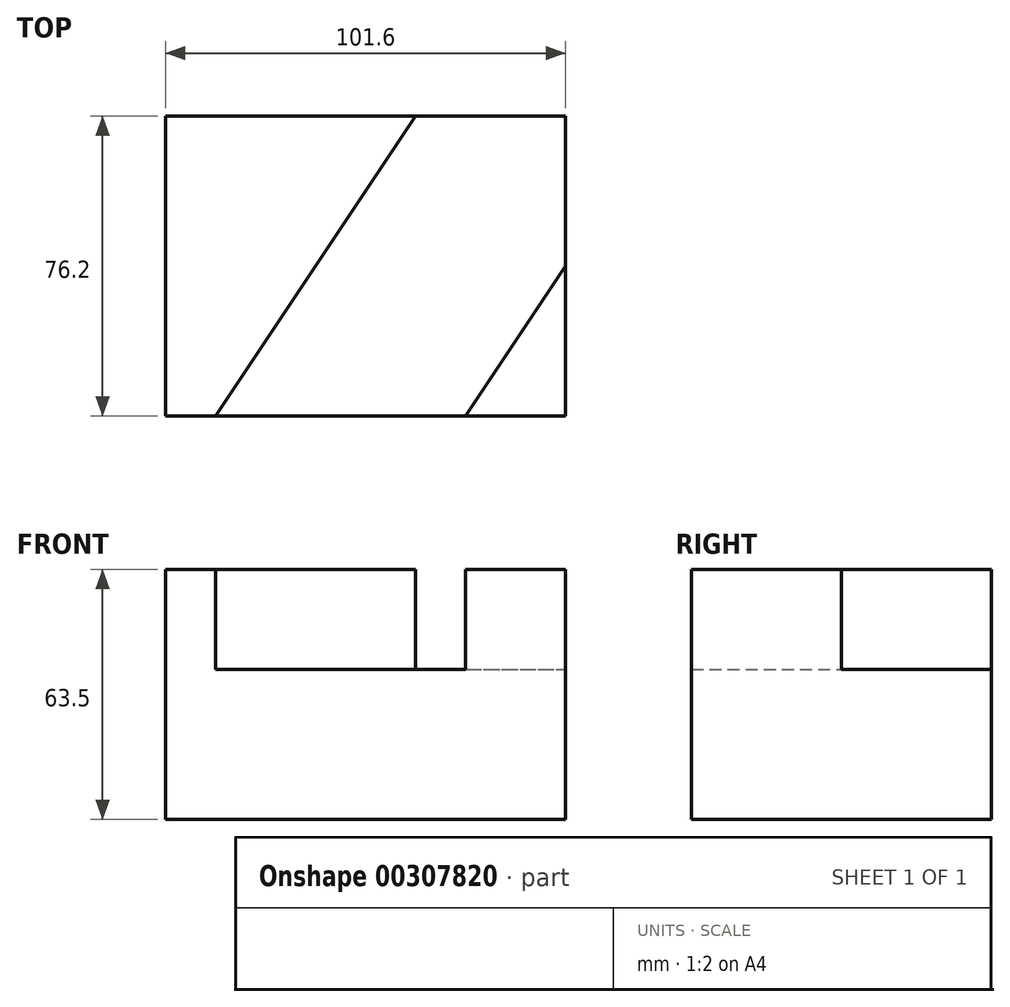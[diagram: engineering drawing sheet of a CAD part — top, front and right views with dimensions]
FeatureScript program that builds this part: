
annotation { "Feature Type Name" : "Feature", "Feature Type Description" : "" }
export const myFeature = defineFeature(function(context is Context, id is Id, definition is map)
    precondition{}
    {
        {
            var Q0;
            Q0=qCreatedBy(makeId("Top.planeOp"),FACE);
            var sketch = newSketch(context, id + "F0", { "sketchPlane" : qUnion([Q0])});
            skLineSegment(sketch, "E0.bottom", {"start": v(-43.22, 25.25) * mm, "end": v(58.38, 25.25) * mm});
            skLineSegment(sketch, "E0.top", {"start": v(-43.22, -50.95) * mm, "end": v(58.38, -50.95) * mm});
            skLineSegment(sketch, "E0.left", {"start": v(-43.22, 25.25) * mm, "end": v(-43.22, -50.95) * mm});
            skLineSegment(sketch, "E0.right", {"start": v(58.38, 25.25) * mm, "end": v(58.38, -50.95) * mm});
            skSolve(sketch);
        }
        {
            var Q0;
            Q0=makeQuery(id+"F0.imprint","IMPRINT",FACE,{"disambiguationData":[TD([[makeQuery(id+"F0.imprint","IMPRINT",EDGE,{"derivedFrom":sQuery(id+"F0.wireOp",EDGE,"E0.bottom")}),-1.0]])]});
            extrude(context, id + "F1", {"entities" : qUnion([Q0]), "depth" : 38.1 * mm});
        }
        {
            var Q0;
            Q0=makeQuery(id+"F1.opExtrude","CAP_FACE",FACE,{"disambiguationData":[OSD([sQuery(id+"F0.wireOp",EDGE,"E0.bottom"),sQuery(id+"F0.wireOp",EDGE,"E0.top"),sQuery(id+"F0.wireOp",EDGE,"E0.left"),sQuery(id+"F0.wireOp",EDGE,"E0.right")])],"isStart":false});
            var sketch = newSketch(context, id + "F2", { "sketchPlane" : qUnion([Q0])});
            skLineSegment(sketch, "E1", {"start": v(32.98, -50.95) * mm, "end": v(58.38, -12.85) * mm});
            skLineSegment(sketch, "E2", {"start": v(58.38, -12.85) * mm, "end": v(58.38, -50.95) * mm});
            skLineSegment(sketch, "E3", {"start": v(58.38, -50.95) * mm, "end": v(32.98, -50.95) * mm});
            skLineSegment(sketch, "E4", {"start": v(-43.22, -50.95) * mm, "end": v(-43.22, 25.25) * mm});
            skLineSegment(sketch, "E5", {"start": v(-43.22, -50.95) * mm, "end": v(-30.52, -50.95) * mm});
            skLineSegment(sketch, "E6", {"start": v(-43.22, 25.25) * mm, "end": v(20.28, 25.25) * mm});
            skLineSegment(sketch, "E7", {"start": v(-30.52, -50.95) * mm, "end": v(20.28, 25.25) * mm});
            skSolve(sketch);
        }
        {
            var Q0;
            Q0=makeQuery(id+"F2.imprint","IMPRINT",FACE,{"disambiguationData":[TD([[makeQuery(id+"F2.imprint","IMPRINT",EDGE,{"derivedFrom":sQuery(id+"F2.wireOp",EDGE,"E4")}),1.0]])]});
            var Q1;
            Q1=makeQuery(id+"F2.imprint","IMPRINT",FACE,{"disambiguationData":[TD([[makeQuery(id+"F2.imprint","IMPRINT",EDGE,{"derivedFrom":sQuery(id+"F2.wireOp",EDGE,"E1")}),-1.0]])]});
            extrude(context, id + "F3", {"entities" : qUnion([Q0, Q1]), "operationType" : NewBodyOperationType.ADD, "depth" : 25.4 * mm});
        }
    });
